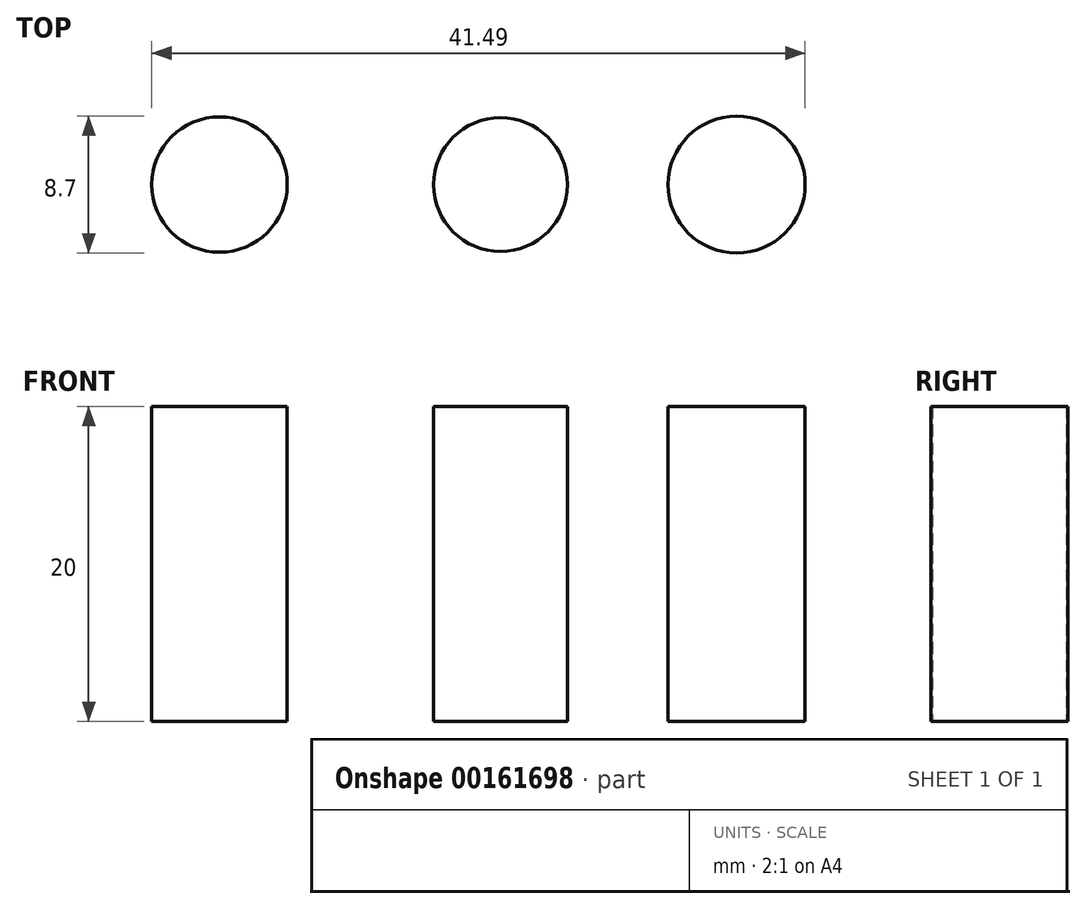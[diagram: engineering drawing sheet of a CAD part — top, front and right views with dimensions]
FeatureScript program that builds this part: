
annotation { "Feature Type Name" : "Feature", "Feature Type Description" : "" }
export const myFeature = defineFeature(function(context is Context, id is Id, definition is map)
    precondition{}
    {
        {
            var Q0;
            Q0=qCreatedBy(makeId("Top.planeOp"),FACE);
            var sketch = newSketch(context, id + "F0", { "sketchPlane" : qUnion([Q0])});
            skCircle(sketch, "E0", {"center": v(0, 0) * mm, "radius": 4.3 * mm});
            skCircle(sketch, "E1", {"center": v(17.85, 0) * mm, "radius": 4.25 * mm});
            skCircle(sketch, "E2", {"center": v(32.84, 0) * mm, "radius": 4.35 * mm});
            skSolve(sketch);
        }
        {
            var Q0;
            Q0 = qSketchRegion(id + "F0", true);
            var Q1;
            Q1=makeQuery(id+"F0.imprint","IMPRINT",FACE,{"disambiguationData":[TD([[makeQuery(id+"F0.imprint","IMPRINT",EDGE,{"derivedFrom":sQuery(id+"F0.wireOp",EDGE,"E0")}),1.0]])]});
            extrude(context, id + "F1", {"entities" : qUnion([Q0, Q1]), "depth" : 20 * mm});
        }
    });
